# Revit family: Water_Heaters_HAJDU_HAJDU-HD-1500-2000_
name_source: partatom
category: Mechanical Equipment
units: mm (PartAtom-declared; Revit-internal decimal feet)

## family parameters
Always vertical = Yes
Classification = None
Cut with Voids When Loaded = No
Maintain Annotation Orientation = No
OmniClass Number = 23.31.29.13
OmniClass Title = Hot Water Tank Heaters
Part Type = Normal
Room Calculation Point = No
Round Connector Dimension = Use Diameter
Shared = No
Work Plane-Based = Yes

## types (2) — shared parameters
Case Material = Hajdu - Felület - Fehér
Csatlakozó magassága "D" = 320 mm  [stored 1.04987 ft]
Církulációs csonk = 50.8 mm  [stored 0.166667 ft]
Default Elevation = 1219.2 mm  [stored 4 ft]
Description = A HD típusú, külső hőcserélővel fűthető tárolók, intézményi, társasházi hőközpontokba, távhőellátási alközpontokba ajánlottak. A melegvíz előállítás átfolyós üzemmódban történik, a tárolónak csúcsigény csillapító, kiegyenlítő szerepe van. A termékcsalád mindegyike nagy nyomásállóságú és nagy átmérőjű csatlakozással rendelkezik.
Elektromos futopatron csatlakozás = 38.1 mm  [stored 0.125 ft]
Homéro csonk = 12.7 mm  [stored 0.0416667 ft]
Korrózióvédelem = tűzzománc + 2db külső áramforrású anód
Manufacturer = HAJDU
Product Page URL = https://hajdurt.hu
Tartály = tűzzománcozott acéllemez
URL = https://hajdurt.hu
Vízcsatlakozás = 50.8 mm  [stored 0.166667 ft]
Üzemi nyomás = 0.8 MPa

## per-type parameters (varying)
| type | Csatlakozó magassága "C" | Csatlakozó magassága "E" | Csatlakozó magassága "F" | Csatlakozó magassága "G" | Csatlakozó magassága "I" | Csatlakozó magassága "J" | Csatlakozó magassága "K" | Csatlakozó magassága "L" | Magasság | Névleges urtartalom | Rádiusz | Tömeg | Átméro | Átméro (szigetelés nélkül) |
| HD 1500 | 525 mm | 1115 mm  [stored 3.65814 ft] | 605 mm  [stored 1.98491 ft] | 1225 mm  [stored 4.01903 ft] | 1225 mm  [stored 4.01903 ft] | 1730 mm  [stored 5.67585 ft] | 1115 mm  [stored 3.65814 ft] | 425 mm  [stored 1.39436 ft] | 2215 mm  [stored 7.26706 ft] | 1500 l | 600 mm  [stored 1.9685 ft] | 350.00 kg | 1200 mm | 1000 mm  [stored 3.28084 ft] |
| HD 2000 | 591 mm  [stored 1.93898 ft] | 1150 mm | 671 mm  [stored 2.20144 ft] | 1321 mm  [stored 4.33399 ft] | 1451 mm | 1581 mm  [stored 5.18701 ft] | 1150 mm | 491 mm  [stored 1.61089 ft] | 2130 mm  [stored 6.98819 ft] | 2000 l | 725 mm  [stored 2.37861 ft] | 482.00 kg | 1450 mm  [stored 4.75722 ft] | 1250 mm  [stored 4.10105 ft] |

note: column(s) folded — value = type name in every type: Model

note: [stored X ft] marks values corroborated as IEEE doubles in the binary element streams (Revit-internal decimal feet)

## geometry (parser evidence)
native form markers: Sweep x4
no freeform markers — native parametric forms only
